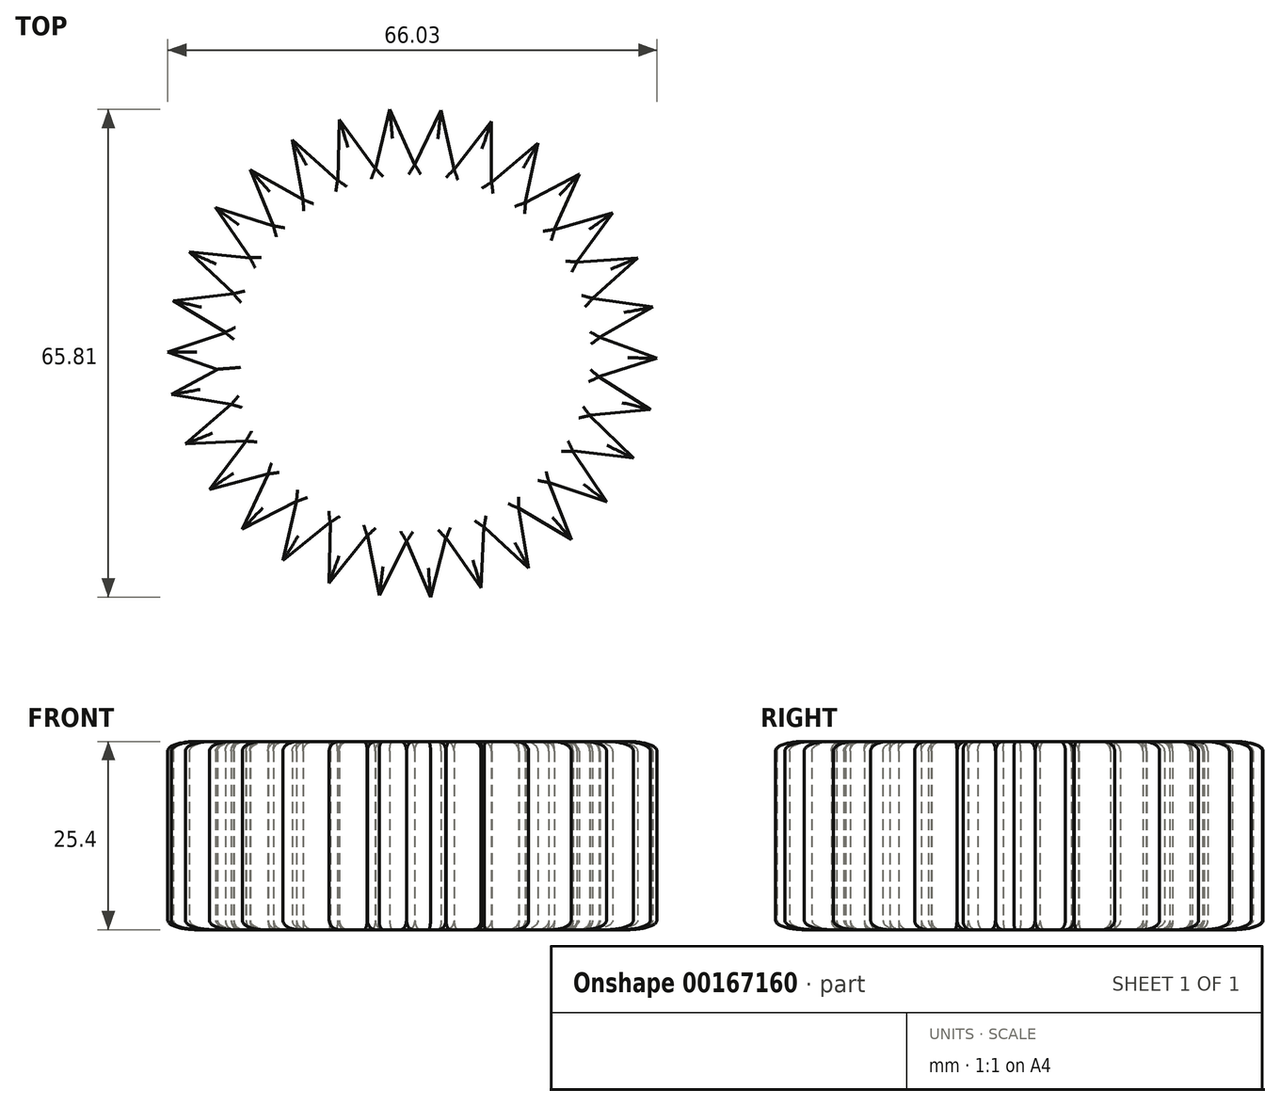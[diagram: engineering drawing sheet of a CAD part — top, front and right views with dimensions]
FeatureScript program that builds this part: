
annotation { "Feature Type Name" : "Feature", "Feature Type Description" : "" }
export const myFeature = defineFeature(function(context is Context, id is Id, definition is map)
    precondition{}
    {
        {
            var Q0;
            Q0=qCreatedBy(makeId("Top.planeOp"),FACE);
            var sketch = newSketch(context, id + "F0", { "sketchPlane" : qUnion([Q0])});
            skCircle(sketch, "E0", {"center": v(0, 0) * mm, "radius": 25.4 * mm});
            skCircle(sketch, "E1.cCircle", {"center": v(0, 0) * mm, "radius": 25.4 * mm, "construction": true});
            skLineSegment(sketch, "E1.0", {"start": v(24.13, -7.94) * mm, "end": v(21.95, -12.78) * mm});
            skLineSegment(sketch, "E1.1", {"start": v(21.95, -12.78) * mm, "end": v(18.81, -17.07) * mm});
            skLineSegment(sketch, "E1.2", {"start": v(18.81, -17.07) * mm, "end": v(14.85, -20.6) * mm});
            skLineSegment(sketch, "E1.3", {"start": v(14.85, -20.6) * mm, "end": v(10.24, -23.24) * mm});
            skLineSegment(sketch, "E1.4", {"start": v(10.24, -23.24) * mm, "end": v(5.19, -24.87) * mm});
            skLineSegment(sketch, "E1.5", {"start": v(5.19, -24.87) * mm, "end": v(-0.1, -25.4) * mm});
            skLineSegment(sketch, "E1.6", {"start": v(-0.1, -25.4) * mm, "end": v(-5.38, -24.82) * mm});
            skLineSegment(sketch, "E1.7", {"start": v(-5.38, -24.82) * mm, "end": v(-10.42, -23.16) * mm});
            skLineSegment(sketch, "E1.8", {"start": v(-10.42, -23.16) * mm, "end": v(-15, -20.5) * mm});
            skLineSegment(sketch, "E1.9", {"start": v(-15, -20.5) * mm, "end": v(-18.94, -16.92) * mm});
            skLineSegment(sketch, "E1.10", {"start": v(-18.94, -16.92) * mm, "end": v(-22.05, -12.62) * mm});
            skLineSegment(sketch, "E1.11", {"start": v(-22.05, -12.62) * mm, "end": v(-24.19, -7.76) * mm});
            skLineSegment(sketch, "E1.12", {"start": v(-24.19, -7.76) * mm, "end": v(-25.27, -2.56) * mm});
            skLineSegment(sketch, "E1.13", {"start": v(-25.27, -2.56) * mm, "end": v(-25.25, 2.75) * mm});
            skLineSegment(sketch, "E1.14", {"start": v(-25.25, 2.75) * mm, "end": v(-24.13, 7.94) * mm});
            skLineSegment(sketch, "E1.15", {"start": v(-24.13, 7.94) * mm, "end": v(-21.95, 12.78) * mm});
            skLineSegment(sketch, "E1.16", {"start": v(-21.95, 12.78) * mm, "end": v(-18.81, 17.07) * mm});
            skLineSegment(sketch, "E1.17", {"start": v(-18.81, 17.07) * mm, "end": v(-14.85, 20.6) * mm});
            skLineSegment(sketch, "E1.18", {"start": v(-14.85, 20.6) * mm, "end": v(-10.24, 23.24) * mm});
            skLineSegment(sketch, "E1.19", {"start": v(-10.24, 23.24) * mm, "end": v(-5.19, 24.87) * mm});
            skLineSegment(sketch, "E1.20", {"start": v(-5.19, 24.87) * mm, "end": v(0.1, 25.4) * mm});
            skLineSegment(sketch, "E1.21", {"start": v(0.1, 25.4) * mm, "end": v(5.38, 24.82) * mm});
            skLineSegment(sketch, "E1.22", {"start": v(5.38, 24.82) * mm, "end": v(10.42, 23.16) * mm});
            skLineSegment(sketch, "E1.23", {"start": v(10.42, 23.16) * mm, "end": v(15, 20.5) * mm});
            skLineSegment(sketch, "E1.24", {"start": v(15, 20.5) * mm, "end": v(18.94, 16.92) * mm});
            skLineSegment(sketch, "E1.25", {"start": v(18.94, 16.92) * mm, "end": v(22.05, 12.62) * mm});
            skLineSegment(sketch, "E1.26", {"start": v(22.05, 12.62) * mm, "end": v(24.19, 7.76) * mm});
            skLineSegment(sketch, "E1.27", {"start": v(24.19, 7.76) * mm, "end": v(25.27, 2.56) * mm});
            skLineSegment(sketch, "E1.28", {"start": v(25.27, 2.56) * mm, "end": v(25.25, -2.75) * mm});
            skLineSegment(sketch, "E1.29", {"start": v(25.25, -2.75) * mm, "end": v(24.13, -7.94) * mm});
            skLineSegment(sketch, "E2", {"start": v(-25.25, 2.75) * mm, "end": v(-33.02, 0.13) * mm});
            skLineSegment(sketch, "E3", {"start": v(-33.02, 0.13) * mm, "end": v(-25.27, -2.56) * mm});
            skLineSegment(sketch, "E4", {"start": v(0, 0) * mm, "end": v(-76.86, 0.3) * mm, "construction": true});
            skLineSegment(sketch, "E5.1.0", {"start": v(-24.12, 7.97) * mm, "end": v(-32.26, 7.03) * mm});
            skLineSegment(sketch, "E5.1.1", {"start": v(-32.26, 7.03) * mm, "end": v(-25.25, 2.78) * mm});
            skLineSegment(sketch, "E5.2.0", {"start": v(-21.92, 12.84) * mm, "end": v(-30.08, 13.62) * mm});
            skLineSegment(sketch, "E5.2.1", {"start": v(-30.08, 13.62) * mm, "end": v(-24.1, 8) * mm});
            skLineSegment(sketch, "E5.3.0", {"start": v(-18.75, 17.14) * mm, "end": v(-26.57, 19.6) * mm});
            skLineSegment(sketch, "E5.3.1", {"start": v(-26.57, 19.6) * mm, "end": v(-21.9, 12.86) * mm});
            skLineSegment(sketch, "E5.4.0", {"start": v(-14.75, 20.68) * mm, "end": v(-21.88, 24.73) * mm});
            skLineSegment(sketch, "E5.4.1", {"start": v(-21.88, 24.73) * mm, "end": v(-18.73, 17.16) * mm});
            skLineSegment(sketch, "E5.5.0", {"start": v(-10.1, 23.3) * mm, "end": v(-16.23, 28.76) * mm});
            skLineSegment(sketch, "E5.5.1", {"start": v(-16.23, 28.76) * mm, "end": v(-14.73, 20.7) * mm});
            skLineSegment(sketch, "E5.6.0", {"start": v(-5, 24.9) * mm, "end": v(-9.86, 31.51) * mm});
            skLineSegment(sketch, "E5.6.1", {"start": v(-9.86, 31.51) * mm, "end": v(-10.07, 23.32) * mm});
            skLineSegment(sketch, "E5.7.0", {"start": v(0.31, 25.4) * mm, "end": v(-3.05, 32.88) * mm});
            skLineSegment(sketch, "E5.7.1", {"start": v(-3.05, 32.88) * mm, "end": v(-4.98, 24.9) * mm});
            skLineSegment(sketch, "E5.8.0", {"start": v(5.62, 24.77) * mm, "end": v(3.9, 32.79) * mm});
            skLineSegment(sketch, "E5.8.1", {"start": v(3.9, 32.79) * mm, "end": v(0.34, 25.4) * mm});
            skLineSegment(sketch, "E5.9.0", {"start": v(10.67, 23.05) * mm, "end": v(10.66, 31.25) * mm});
            skLineSegment(sketch, "E5.9.1", {"start": v(10.66, 31.25) * mm, "end": v(5.65, 24.76) * mm});
            skLineSegment(sketch, "E5.10.0", {"start": v(15.25, 20.3) * mm, "end": v(16.96, 28.33) * mm});
            skLineSegment(sketch, "E5.10.1", {"start": v(16.96, 28.33) * mm, "end": v(10.7, 23.04) * mm});
            skLineSegment(sketch, "E5.11.0", {"start": v(19.16, 16.67) * mm, "end": v(22.51, 24.16) * mm});
            skLineSegment(sketch, "E5.11.1", {"start": v(22.51, 24.16) * mm, "end": v(15.28, 20.3) * mm});
            skLineSegment(sketch, "E5.12.0", {"start": v(22.23, 12.3) * mm, "end": v(27.06, 18.92) * mm});
            skLineSegment(sketch, "E5.12.1", {"start": v(27.06, 18.92) * mm, "end": v(19.18, 16.65) * mm});
            skLineSegment(sketch, "E5.13.0", {"start": v(24.3, 7.38) * mm, "end": v(30.42, 12.84) * mm});
            skLineSegment(sketch, "E5.13.1", {"start": v(30.42, 12.84) * mm, "end": v(22.24, 12.27) * mm});
            skLineSegment(sketch, "E5.14.0", {"start": v(25.31, 2.13) * mm, "end": v(32.43, 6.2) * mm});
            skLineSegment(sketch, "E5.14.1", {"start": v(32.43, 6.2) * mm, "end": v(24.31, 7.35) * mm});
            skLineSegment(sketch, "E5.15.0", {"start": v(25.2, -3.2) * mm, "end": v(33.01, -0.72) * mm});
            skLineSegment(sketch, "E5.15.1", {"start": v(33.01, -0.72) * mm, "end": v(25.31, 2.1) * mm});
            skLineSegment(sketch, "E5.16.0", {"start": v(23.97, -8.4) * mm, "end": v(32.13, -7.6) * mm});
            skLineSegment(sketch, "E5.16.1", {"start": v(32.13, -7.6) * mm, "end": v(25.2, -3.24) * mm});
            skLineSegment(sketch, "E5.17.0", {"start": v(21.68, -13.23) * mm, "end": v(29.83, -14.16) * mm});
            skLineSegment(sketch, "E5.17.1", {"start": v(29.83, -14.16) * mm, "end": v(23.96, -8.43) * mm});
            skLineSegment(sketch, "E5.18.0", {"start": v(18.44, -17.47) * mm, "end": v(26.2, -20.08) * mm});
            skLineSegment(sketch, "E5.18.1", {"start": v(26.2, -20.08) * mm, "end": v(21.67, -13.26) * mm});
            skLineSegment(sketch, "E5.19.0", {"start": v(14.38, -20.94) * mm, "end": v(21.43, -25.12) * mm});
            skLineSegment(sketch, "E5.19.1", {"start": v(21.43, -25.12) * mm, "end": v(18.42, -17.5) * mm});
            skLineSegment(sketch, "E5.20.0", {"start": v(9.68, -23.48) * mm, "end": v(15.7, -29.05) * mm});
            skLineSegment(sketch, "E5.20.1", {"start": v(15.7, -29.05) * mm, "end": v(14.35, -20.96) * mm});
            skLineSegment(sketch, "E5.21.0", {"start": v(4.56, -24.99) * mm, "end": v(9.28, -31.69) * mm});
            skLineSegment(sketch, "E5.21.1", {"start": v(9.28, -31.69) * mm, "end": v(9.65, -23.5) * mm});
            skLineSegment(sketch, "E5.22.0", {"start": v(-0.77, -25.39) * mm, "end": v(2.45, -32.93) * mm});
            skLineSegment(sketch, "E5.22.1", {"start": v(2.45, -32.93) * mm, "end": v(4.53, -25) * mm});
            skLineSegment(sketch, "E5.23.0", {"start": v(-6.06, -24.67) * mm, "end": v(-4.49, -32.71) * mm});
            skLineSegment(sketch, "E5.23.1", {"start": v(-4.49, -32.71) * mm, "end": v(-0.8, -25.39) * mm});
            skLineSegment(sketch, "E5.24.0", {"start": v(-11.09, -22.85) * mm, "end": v(-11.23, -31.05) * mm});
            skLineSegment(sketch, "E5.24.1", {"start": v(-11.23, -31.05) * mm, "end": v(-6.1, -24.66) * mm});
            skLineSegment(sketch, "E5.25.0", {"start": v(-15.62, -20.03) * mm, "end": v(-17.47, -28.02) * mm});
            skLineSegment(sketch, "E5.25.1", {"start": v(-17.47, -28.02) * mm, "end": v(-11.11, -22.84) * mm});
            skLineSegment(sketch, "E5.26.0", {"start": v(-19.46, -16.32) * mm, "end": v(-22.94, -23.75) * mm});
            skLineSegment(sketch, "E5.26.1", {"start": v(-22.94, -23.75) * mm, "end": v(-15.64, -20.01) * mm});
            skLineSegment(sketch, "E5.27.0", {"start": v(-22.44, -11.9) * mm, "end": v(-27.4, -18.43) * mm});
            skLineSegment(sketch, "E5.27.1", {"start": v(-27.4, -18.43) * mm, "end": v(-19.48, -16.3) * mm});
            skLineSegment(sketch, "E5.28.0", {"start": v(-24.43, -6.94) * mm, "end": v(-30.65, -12.29) * mm});
            skLineSegment(sketch, "E5.28.1", {"start": v(-30.65, -12.29) * mm, "end": v(-22.46, -11.87) * mm});
            skLineSegment(sketch, "E5.29.0", {"start": v(-25.34, -1.67) * mm, "end": v(-32.54, -5.6) * mm});
            skLineSegment(sketch, "E5.29.1", {"start": v(-32.54, -5.6) * mm, "end": v(-24.44, -6.9) * mm});
            skLineSegment(sketch, "E5.anchor1", {"start": v(0, 0) * mm, "end": v(-33.02, 0.13) * mm, "construction": true});
            skLineSegment(sketch, "E5.anchor2", {"start": v(0, 0) * mm, "end": v(-32.54, -5.6) * mm, "construction": true});
            skSolve(sketch);
        }
        {
            var Q0;
            Q0 = qSketchRegion(id + "F0", true);
            extrude(context, id + "F1", {"entities" : qUnion([Q0]), "depth" : 25.4 * mm});
        }
        {
            var Q0;
            Q0=makeQuery(id+"F1.opExtrude","CAP_FACE",FACE,{"disambiguationData":[OSD([sQuery(id+"F0.wireOp",EDGE,"E0"),sQuery(id+"F0.wireOp",EDGE,"E2"),sQuery(id+"F0.wireOp",EDGE,"E3"),sQuery(id+"F0.wireOp",EDGE,"E5.1.0"),sQuery(id+"F0.wireOp",EDGE,"E5.1.1"),sQuery(id+"F0.wireOp",EDGE,"E5.2.0"),sQuery(id+"F0.wireOp",EDGE,"E5.2.1"),sQuery(id+"F0.wireOp",EDGE,"E5.3.0"),sQuery(id+"F0.wireOp",EDGE,"E5.3.1"),sQuery(id+"F0.wireOp",EDGE,"E5.4.0"),sQuery(id+"F0.wireOp",EDGE,"E5.4.1"),sQuery(id+"F0.wireOp",EDGE,"E5.5.0"),sQuery(id+"F0.wireOp",EDGE,"E5.5.1"),sQuery(id+"F0.wireOp",EDGE,"E5.6.0"),sQuery(id+"F0.wireOp",EDGE,"E5.6.1"),sQuery(id+"F0.wireOp",EDGE,"E5.7.0"),sQuery(id+"F0.wireOp",EDGE,"E5.7.1"),sQuery(id+"F0.wireOp",EDGE,"E5.8.0"),sQuery(id+"F0.wireOp",EDGE,"E5.8.1"),sQuery(id+"F0.wireOp",EDGE,"E5.9.0"),sQuery(id+"F0.wireOp",EDGE,"E5.9.1"),sQuery(id+"F0.wireOp",EDGE,"E5.10.0"),sQuery(id+"F0.wireOp",EDGE,"E5.10.1"),sQuery(id+"F0.wireOp",EDGE,"E5.11.0"),sQuery(id+"F0.wireOp",EDGE,"E5.11.1"),sQuery(id+"F0.wireOp",EDGE,"E5.12.0"),sQuery(id+"F0.wireOp",EDGE,"E5.12.1"),sQuery(id+"F0.wireOp",EDGE,"E5.13.0"),sQuery(id+"F0.wireOp",EDGE,"E5.13.1"),sQuery(id+"F0.wireOp",EDGE,"E5.14.0"),sQuery(id+"F0.wireOp",EDGE,"E5.14.1"),sQuery(id+"F0.wireOp",EDGE,"E5.15.0"),sQuery(id+"F0.wireOp",EDGE,"E5.15.1"),sQuery(id+"F0.wireOp",EDGE,"E5.16.0"),sQuery(id+"F0.wireOp",EDGE,"E5.16.1"),sQuery(id+"F0.wireOp",EDGE,"E5.17.0"),sQuery(id+"F0.wireOp",EDGE,"E5.17.1"),sQuery(id+"F0.wireOp",EDGE,"E5.18.0"),sQuery(id+"F0.wireOp",EDGE,"E5.18.1"),sQuery(id+"F0.wireOp",EDGE,"E5.19.0"),sQuery(id+"F0.wireOp",EDGE,"E5.19.1"),sQuery(id+"F0.wireOp",EDGE,"E5.20.0"),sQuery(id+"F0.wireOp",EDGE,"E5.20.1"),sQuery(id+"F0.wireOp",EDGE,"E5.21.0"),sQuery(id+"F0.wireOp",EDGE,"E5.21.1"),sQuery(id+"F0.wireOp",EDGE,"E5.22.0"),sQuery(id+"F0.wireOp",EDGE,"E5.22.1"),sQuery(id+"F0.wireOp",EDGE,"E5.23.0"),sQuery(id+"F0.wireOp",EDGE,"E5.23.1"),sQuery(id+"F0.wireOp",EDGE,"E5.24.0"),sQuery(id+"F0.wireOp",EDGE,"E5.24.1"),sQuery(id+"F0.wireOp",EDGE,"E5.25.0"),sQuery(id+"F0.wireOp",EDGE,"E5.25.1"),sQuery(id+"F0.wireOp",EDGE,"E5.26.0"),sQuery(id+"F0.wireOp",EDGE,"E5.26.1"),sQuery(id+"F0.wireOp",EDGE,"E5.27.0"),sQuery(id+"F0.wireOp",EDGE,"E5.27.1"),sQuery(id+"F0.wireOp",EDGE,"E5.28.0"),sQuery(id+"F0.wireOp",EDGE,"E5.28.1"),sQuery(id+"F0.wireOp",EDGE,"E5.29.0"),sQuery(id+"F0.wireOp",EDGE,"E5.29.1")])],"isStart":true});
            var Q1;
            Q1=makeQuery(id+"F1.opExtrude","CAP_FACE",FACE,{"disambiguationData":[OSD([sQuery(id+"F0.wireOp",EDGE,"E0"),sQuery(id+"F0.wireOp",EDGE,"E2"),sQuery(id+"F0.wireOp",EDGE,"E3"),sQuery(id+"F0.wireOp",EDGE,"E5.1.0"),sQuery(id+"F0.wireOp",EDGE,"E5.1.1"),sQuery(id+"F0.wireOp",EDGE,"E5.2.0"),sQuery(id+"F0.wireOp",EDGE,"E5.2.1"),sQuery(id+"F0.wireOp",EDGE,"E5.3.0"),sQuery(id+"F0.wireOp",EDGE,"E5.3.1"),sQuery(id+"F0.wireOp",EDGE,"E5.4.0"),sQuery(id+"F0.wireOp",EDGE,"E5.4.1"),sQuery(id+"F0.wireOp",EDGE,"E5.5.0"),sQuery(id+"F0.wireOp",EDGE,"E5.5.1"),sQuery(id+"F0.wireOp",EDGE,"E5.6.0"),sQuery(id+"F0.wireOp",EDGE,"E5.6.1"),sQuery(id+"F0.wireOp",EDGE,"E5.7.0"),sQuery(id+"F0.wireOp",EDGE,"E5.7.1"),sQuery(id+"F0.wireOp",EDGE,"E5.8.0"),sQuery(id+"F0.wireOp",EDGE,"E5.8.1"),sQuery(id+"F0.wireOp",EDGE,"E5.9.0"),sQuery(id+"F0.wireOp",EDGE,"E5.9.1"),sQuery(id+"F0.wireOp",EDGE,"E5.10.0"),sQuery(id+"F0.wireOp",EDGE,"E5.10.1"),sQuery(id+"F0.wireOp",EDGE,"E5.11.0"),sQuery(id+"F0.wireOp",EDGE,"E5.11.1"),sQuery(id+"F0.wireOp",EDGE,"E5.12.0"),sQuery(id+"F0.wireOp",EDGE,"E5.12.1"),sQuery(id+"F0.wireOp",EDGE,"E5.13.0"),sQuery(id+"F0.wireOp",EDGE,"E5.13.1"),sQuery(id+"F0.wireOp",EDGE,"E5.14.0"),sQuery(id+"F0.wireOp",EDGE,"E5.14.1"),sQuery(id+"F0.wireOp",EDGE,"E5.15.0"),sQuery(id+"F0.wireOp",EDGE,"E5.15.1"),sQuery(id+"F0.wireOp",EDGE,"E5.16.0"),sQuery(id+"F0.wireOp",EDGE,"E5.16.1"),sQuery(id+"F0.wireOp",EDGE,"E5.17.0"),sQuery(id+"F0.wireOp",EDGE,"E5.17.1"),sQuery(id+"F0.wireOp",EDGE,"E5.18.0"),sQuery(id+"F0.wireOp",EDGE,"E5.18.1"),sQuery(id+"F0.wireOp",EDGE,"E5.19.0"),sQuery(id+"F0.wireOp",EDGE,"E5.19.1"),sQuery(id+"F0.wireOp",EDGE,"E5.20.0"),sQuery(id+"F0.wireOp",EDGE,"E5.20.1"),sQuery(id+"F0.wireOp",EDGE,"E5.21.0"),sQuery(id+"F0.wireOp",EDGE,"E5.21.1"),sQuery(id+"F0.wireOp",EDGE,"E5.22.0"),sQuery(id+"F0.wireOp",EDGE,"E5.22.1"),sQuery(id+"F0.wireOp",EDGE,"E5.23.0"),sQuery(id+"F0.wireOp",EDGE,"E5.23.1"),sQuery(id+"F0.wireOp",EDGE,"E5.24.0"),sQuery(id+"F0.wireOp",EDGE,"E5.24.1"),sQuery(id+"F0.wireOp",EDGE,"E5.25.0"),sQuery(id+"F0.wireOp",EDGE,"E5.25.1"),sQuery(id+"F0.wireOp",EDGE,"E5.26.0"),sQuery(id+"F0.wireOp",EDGE,"E5.26.1"),sQuery(id+"F0.wireOp",EDGE,"E5.27.0"),sQuery(id+"F0.wireOp",EDGE,"E5.27.1"),sQuery(id+"F0.wireOp",EDGE,"E5.28.0"),sQuery(id+"F0.wireOp",EDGE,"E5.28.1"),sQuery(id+"F0.wireOp",EDGE,"E5.29.0"),sQuery(id+"F0.wireOp",EDGE,"E5.29.1")])],"isStart":false});
            fillet(context, id + "F2", {"entities" : qUnion([Q0, Q1]), "radius" : 1.27 * mm, "tangentPropagation" : true, "allowEdgeOverflow" : false});
        }
    });
